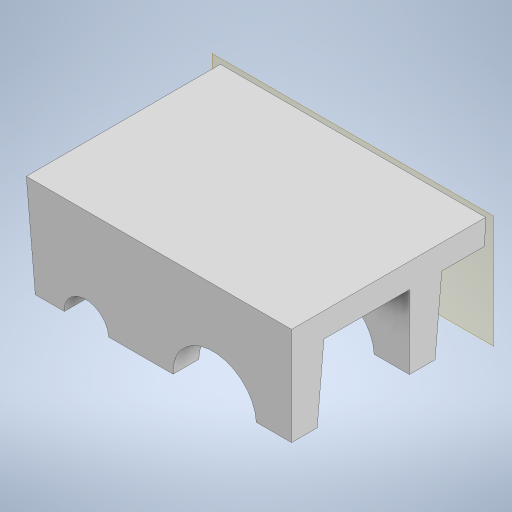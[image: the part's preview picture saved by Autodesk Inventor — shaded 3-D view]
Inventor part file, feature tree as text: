
AUTODESK INVENTOR PART (.ipt)
format: ipt  version: 2023 (Build 270158000, 158)  size: 279,040 bytes
history: native  units: in
note: dims shown in document units (in); Inventor stores cm internally (conversion verified against a paired STEP export)
features: extrude x3, sketch x2, plane x1, draft x1
ambient origin geometry x8: Origin, YZ Plane, XZ Plane, XY Plane, X Axis, Y Axis, Z Axis, Center Point
bodies: Solid1 (feature_tree)
feature tree (7):
  extrude  "Extrusion1"  Depth=5.0in
  extrude  "Extrusion2"  Depth=0.5in
  plane  "Work Plane1"
  sketch  "Sketch5"  dims[d3=7.4in d4=0.0in d15=1.4in d16=3.7in d17=6.0in d18=0.5in d20=2.528in d21=7.4in d22=0.0in d25=1.5in d26=0.866in d31=1.2546in d32=0.5669in d33=2.0in d34=1.5in d35=0.0172in d36=9.0in d37=0.0in d27=0.5in d28=0.0344in d29=0.0in d30=0.0in d38=0.5in d39=0.0344in]
  draft  "FaceDraft1"
  extrude  "Extrusion5"  Depth=0.5in
  sketch  "Sketch1"  dims[d0=5.0in d2=1.625in]
